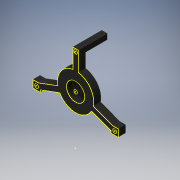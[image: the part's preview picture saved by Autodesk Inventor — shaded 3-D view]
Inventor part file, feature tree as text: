
AUTODESK INVENTOR PART (.ipt)
format: ipt  version: 2016 (Build 200138000, 138)  size: 207,360 bytes
history: native  units: mm
features: extrude x5, sketch x3, other x1, projected_geometry x1
ambient origin geometry x8: Origin, YZ Plane, XZ Plane, XY Plane, X Axis, Y Axis, Z Axis, Center Point
bodies: Body1 (feature_tree)
feature tree (10):
  other  "ソリッド1"
  extrude  "押し出し1"  Depth=32.0mm
  extrude  "押し出し3"  Depth=2.0mm
  sketch  "スケッチ6"
  extrude  "押し出し7"  Depth=27.0mm
  extrude  "押し出し9"  Depth=30.0mm
  extrude  "押し出し10"  Depth=3.0mm
  sketch  "スケッチ8"
  sketch  "スケッチ7"
  projected_geometry  "投影ループ1"
